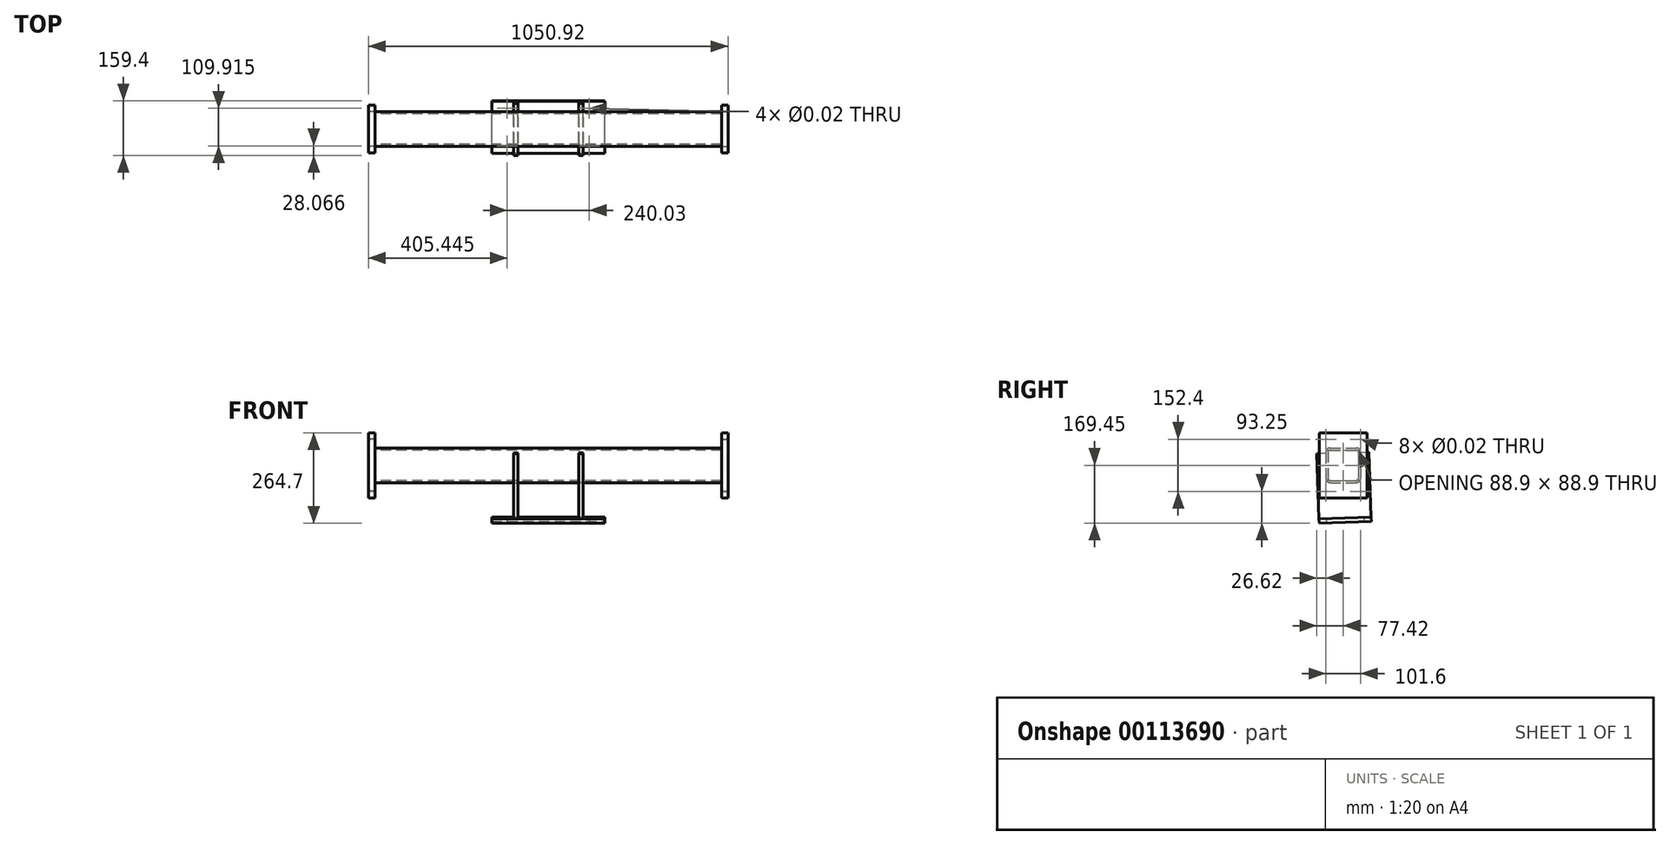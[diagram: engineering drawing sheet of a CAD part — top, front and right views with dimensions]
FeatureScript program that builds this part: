
annotation { "Feature Type Name" : "Feature", "Feature Type Description" : "" }
export const myFeature = defineFeature(function(context is Context, id is Id, definition is map)
    precondition{}
    {
        {
            var Q0;
            Q0=qCreatedBy(makeId("Right.planeOp"),FACE);
            var sketch = newSketch(context, id + "F0", { "sketchPlane" : qUnion([Q0])});
            skLineSegment(sketch, "E0.bottom", {"start": v(-38.1, 50.8) * mm, "end": v(38.1, 50.8) * mm});
            skLineSegment(sketch, "E0.top", {"start": v(-38.1, -50.8) * mm, "end": v(38.1, -50.8) * mm});
            skLineSegment(sketch, "E0.left", {"start": v(-50.8, 38.1) * mm, "end": v(-50.8, -38.1) * mm});
            skLineSegment(sketch, "E0.right", {"start": v(50.8, 38.1) * mm, "end": v(50.8, -38.1) * mm});
            skPoint(sketch, "E0.middle", {"position": v(0, 0) * mm});
            skPoint(sketch, "E1.visualSharp", {"position": v(-50.8, 50.8) * mm});
            skArc(sketch, "E1.filletArc", {"start": v(-38.1, 50.8) * mm, "mid": v(-47.08, 47.08) * mm, "end": v(-50.8, 38.1) * mm});
            skPoint(sketch, "E2.visualSharp", {"position": v(50.8, 50.8) * mm});
            skArc(sketch, "E2.filletArc", {"start": v(50.8, 38.1) * mm, "mid": v(47.08, 47.08) * mm, "end": v(38.1, 50.8) * mm});
            skPoint(sketch, "E3.visualSharp", {"position": v(50.8, -50.8) * mm});
            skArc(sketch, "E3.filletArc", {"start": v(38.1, -50.8) * mm, "mid": v(47.08, -47.08) * mm, "end": v(50.8, -38.1) * mm});
            skPoint(sketch, "E4.visualSharp", {"position": v(-50.8, -50.8) * mm});
            skArc(sketch, "E4.filletArc", {"start": v(-50.8, -38.1) * mm, "mid": v(-47.08, -47.08) * mm, "end": v(-38.1, -50.8) * mm});
            skArc(sketch, "E5.0", {"start": v(-38.1, 44.45) * mm, "mid": v(-42.6, 42.6) * mm, "end": v(-44.45, 38.1) * mm});
            skLineSegment(sketch, "E5.1", {"start": v(-44.45, 38.1) * mm, "end": v(-44.45, -38.1) * mm});
            skLineSegment(sketch, "E5.2", {"start": v(-38.1, 44.45) * mm, "end": v(38.1, 44.45) * mm});
            skArc(sketch, "E5.3", {"start": v(-44.45, -38.1) * mm, "mid": v(-42.6, -42.6) * mm, "end": v(-38.1, -44.45) * mm});
            skArc(sketch, "E5.4", {"start": v(44.45, 38.1) * mm, "mid": v(42.6, 42.6) * mm, "end": v(38.1, 44.45) * mm});
            skLineSegment(sketch, "E5.5", {"start": v(44.45, 38.1) * mm, "end": v(44.45, -38.1) * mm});
            skArc(sketch, "E5.6", {"start": v(38.1, -44.45) * mm, "mid": v(42.6, -42.6) * mm, "end": v(44.45, -38.1) * mm});
            skLineSegment(sketch, "E5.7", {"start": v(-38.1, -44.45) * mm, "end": v(38.1, -44.45) * mm});
            skSolve(sketch);
        }
        {
            var Q0;
            Q0 = qSketchRegion(id + "F0", true);
            extrude(context, id + "F1", {"entities" : qUnion([Q0]), "endBound" : BoundingType.SYMMETRIC, "depth" : 1012.82 * mm});
        }
        {
            var Q0;
            Q0=makeQuery(id+"F1.opExtrude","CAP_FACE",FACE,{"disambiguationData":[OSD([sQuery(id+"F0.wireOp",EDGE,"E0.bottom"),sQuery(id+"F0.wireOp",EDGE,"E0.top"),sQuery(id+"F0.wireOp",EDGE,"E0.left"),sQuery(id+"F0.wireOp",EDGE,"E0.right"),sQuery(id+"F0.wireOp",EDGE,"E1.filletArc"),sQuery(id+"F0.wireOp",EDGE,"E2.filletArc"),sQuery(id+"F0.wireOp",EDGE,"E3.filletArc"),sQuery(id+"F0.wireOp",EDGE,"E4.filletArc"),sQuery(id+"F0.wireOp",EDGE,"E5.0"),sQuery(id+"F0.wireOp",EDGE,"E5.1"),sQuery(id+"F0.wireOp",EDGE,"E5.2"),sQuery(id+"F0.wireOp",EDGE,"E5.3"),sQuery(id+"F0.wireOp",EDGE,"E5.4"),sQuery(id+"F0.wireOp",EDGE,"E5.5"),sQuery(id+"F0.wireOp",EDGE,"E5.6"),sQuery(id+"F0.wireOp",EDGE,"E5.7")])],"isStart":false});
            var sketch = newSketch(context, id + "F2", { "sketchPlane" : qUnion([Q0])});
            skLineSegment(sketch, "E6.bottom", {"start": v(-69.85, 95.25) * mm, "end": v(69.85, 95.25) * mm});
            skLineSegment(sketch, "E6.top", {"start": v(-69.85, -95.25) * mm, "end": v(69.85, -95.25) * mm});
            skLineSegment(sketch, "E6.left", {"start": v(-69.85, 95.25) * mm, "end": v(-69.85, -95.25) * mm});
            skLineSegment(sketch, "E6.right", {"start": v(69.85, 95.25) * mm, "end": v(69.85, -95.25) * mm});
            skPoint(sketch, "E6.middle", {"position": v(0, 0) * mm});
            skSolve(sketch);
        }
        {
            var Q0;
            Q0 = qSketchRegion(id + "F2", true);
            extrude(context, id + "F3", {"entities" : qUnion([Q0]), "depth" : 19.05 * mm});
        }
        {
            var Q0;
            Q0=makeQuery(id+"F3.opExtrude","CAP_FACE",FACE,{"disambiguationData":[OSD([sQuery(id+"F2.wireOp",EDGE,"E6.bottom"),sQuery(id+"F2.wireOp",EDGE,"E6.top"),sQuery(id+"F2.wireOp",EDGE,"E6.left"),sQuery(id+"F2.wireOp",EDGE,"E6.right")])],"isStart":false});
            var sketch = newSketch(context, id + "F4", { "sketchPlane" : qUnion([Q0])});
            skLineSegment(sketch, "E7.bottom", {"start": v(-50.8, 76.2) * mm, "end": v(50.8, 76.2) * mm, "construction": true});
            skLineSegment(sketch, "E7.top", {"start": v(-50.8, -76.2) * mm, "end": v(50.8, -76.2) * mm, "construction": true});
            skLineSegment(sketch, "E7.left", {"start": v(-50.8, 76.2) * mm, "end": v(-50.8, -76.2) * mm, "construction": true});
            skLineSegment(sketch, "E7.right", {"start": v(50.8, 76.2) * mm, "end": v(50.8, -76.2) * mm, "construction": true});
            skPoint(sketch, "E7.middle", {"position": v(0, 0) * mm});
            skPoint(sketch, "E8", {"position": v(-50.8, 76.2) * mm});
            skPoint(sketch, "E9", {"position": v(50.8, 76.2) * mm});
            skPoint(sketch, "E10", {"position": v(50.8, -76.2) * mm});
            skPoint(sketch, "E11", {"position": v(-50.8, -76.2) * mm});
            skSolve(sketch);
        }
        {
            var Q0;
            Q0=sQuery(id+"F4.wireOp",VERTEX,"E8");
            var Q1;
            Q1=sQuery(id+"F4.wireOp",VERTEX,"E9");
            var Q2;
            Q2=sQuery(id+"F4.wireOp",VERTEX,"E11");
            var Q3;
            Q3=sQuery(id+"F4.wireOp",VERTEX,"E10");
            var Q4;
            Q4=makeQuery(id+"F3.opExtrude","SWEPT_BODY",BODY,{"disambiguationData":[OSD([sQuery(id+"F2.wireOp",EDGE,"E6.bottom"),sQuery(id+"F2.wireOp",EDGE,"E6.top"),sQuery(id+"F2.wireOp",EDGE,"E6.left"),sQuery(id+"F2.wireOp",EDGE,"E6.right")])]});
            hole(context, id + "F5", {"style" : HoleStyle.SIMPLE, "endStyle" : HoleEndStyle.THROUGH, "standardTappedOrClearance" : lookupTablePath({ "standard" : "ANSI", "size" : "5/8 (0.62)", "type" : "Drilled" }), "standardBlindInLast" : lookupTablePath({ "standard" : "ANSI", "size" : "5/8", "type" : "Drilled" }), "holeDiameter" : 5 / 203.2 * mm, "locations" : qUnion([Q0, Q1, Q2, Q3]), "scope" : qUnion([Q4]), "isTappedThrough" : true});
        }
        {
            var Q0;
            Q0=makeQuery(id+"F3.opExtrude","SWEPT_BODY",BODY,{"disambiguationData":[OSD([sQuery(id+"F2.wireOp",EDGE,"E6.bottom"),sQuery(id+"F2.wireOp",EDGE,"E6.top"),sQuery(id+"F2.wireOp",EDGE,"E6.left"),sQuery(id+"F2.wireOp",EDGE,"E6.right")])]});
            var Q1;
            Q1=qCreatedBy(makeId("Right.planeOp"),FACE);
            mirror(context, id + "F6", {"entities" : qUnion([Q0]), "mirrorPlane" : qUnion([Q1])});
        }
        {
            var Q0;
            Q0=qCreatedBy(makeId("Right.planeOp"),FACE);
            cPlane(context, id + "F7", {"entities" : qUnion([Q0]), "cplaneType" : CPlaneType.OFFSET, "offset" : 88.9 * mm, "width" : 152.4 * mm, "height" : 152.4 * mm});
        }
        {
            var Q0;
            Q0=qCreatedBy(id+"F7.planeOp",FACE);
            var sketch = newSketch(context, id + "F8", { "sketchPlane" : qUnion([Q0])});
            skLineSegment(sketch, "E12", {"start": v(0, 0) * mm, "end": v(10.06, -288.01) * mm, "construction": true});
            skLineSegment(sketch, "E13", {"start": v(0, 0) * mm, "end": v(0, -287.93) * mm, "construction": true});
            skLineSegment(sketch, "E14.0", {"start": v(74.89, 38.94) * mm, "end": v(81.53, -151.44) * mm});
            skLineSegment(sketch, "E15.0", {"start": v(50.8, 38.1) * mm, "end": v(50.8, -38.1) * mm});
            skLineSegment(sketch, "E16.0", {"start": v(-50.8, 38.1) * mm, "end": v(-50.8, -38.1) * mm});
            skLineSegment(sketch, "E17", {"start": v(-133, 38.1) * mm, "end": v(-50.8, 38.1) * mm, "construction": true});
            skLineSegment(sketch, "E18.trimOffspring", {"start": v(50.8, 38.1) * mm, "end": v(138.85, 38.1) * mm, "construction": true});
            skLineSegment(sketch, "E19.MirrorCS", {"start": v(-77.42, 33.62) * mm, "end": v(-70.77, -156.76) * mm});
            skLineSegment(sketch, "E20", {"start": v(81.53, -151.44) * mm, "end": v(-70.77, -156.76) * mm});
            skLineSegment(sketch, "E21.0", {"start": v(-50.8, 34.55) * mm, "end": v(-77.42, 33.62) * mm});
            skPoint(sketch, "E22.orphan", {"position": v(76.15, 2.66) * mm});
            skLineSegment(sketch, "E23", {"start": v(50.8, 38.1) * mm, "end": v(74.89, 38.94) * mm});
            skPoint(sketch, "E24.orphan", {"position": v(86.21, -285.35) * mm});
            skPoint(sketch, "E25.orphan", {"position": v(-66.1, -290.67) * mm});
            skPoint(sketch, "E26.orphan", {"position": v(-76.15, -2.66) * mm});
            skArc(sketch, "E27.0", {"start": v(-50.8, -38.1) * mm, "mid": v(-47.08, -47.08) * mm, "end": v(-38.1, -50.8) * mm});
            skLineSegment(sketch, "E28.0", {"start": v(-38.1, -50.8) * mm, "end": v(38.1, -50.8) * mm});
            skArc(sketch, "E29.0", {"start": v(38.1, -50.8) * mm, "mid": v(47.08, -47.08) * mm, "end": v(50.8, -38.1) * mm});
            skSolve(sketch);
        }
        {
            var Q0;
            Q0 = qSketchRegion(id + "F8", true);
            extrude(context, id + "F9", {"entities" : qUnion([Q0]), "depth" : 12.7 * mm});
        }
        {
            var Q0;
            Q0=makeQuery(id+"F9.opExtrude","SWEPT_BODY",BODY,{"disambiguationData":[OSD([sQuery(id+"F8.wireOp",EDGE,"E14.0"),sQuery(id+"F8.wireOp",EDGE,"E15.0"),sQuery(id+"F8.wireOp",EDGE,"E16.0"),sQuery(id+"F8.wireOp",EDGE,"E19.MirrorCS"),sQuery(id+"F8.wireOp",EDGE,"E20"),sQuery(id+"F8.wireOp",EDGE,"E21.0"),sQuery(id+"F8.wireOp",EDGE,"E23"),sQuery(id+"F8.wireOp",EDGE,"E27.0"),sQuery(id+"F8.wireOp",EDGE,"E28.0"),sQuery(id+"F8.wireOp",EDGE,"E29.0")])]});
            var Q1;
            Q1=qCreatedBy(makeId("Right.planeOp"),FACE);
            mirror(context, id + "F10", {"entities" : qUnion([Q0]), "mirrorPlane" : qUnion([Q1])});
        }
        {
            var Q0;
            Q0=makeQuery(id+"F9.opExtrude","SWEPT_FACE",FACE,{"disambiguationData":[OSD([sQuery(id+"F8.wireOp",EDGE,"E20")])]});
            var sketch = newSketch(context, id + "F11", { "sketchPlane" : qUnion([Q0])});
            skLineSegment(sketch, "E30.0.0", {"start": v(-88.9, -76.2) * mm, "end": v(-88.9, 76.2) * mm, "construction": true});
            skLineSegment(sketch, "E30.0.1", {"start": v(-88.9, 76.2) * mm, "end": v(-101.6, 76.2) * mm, "construction": true});
            skLineSegment(sketch, "E30.0.2", {"start": v(-101.6, 76.2) * mm, "end": v(-101.6, -76.2) * mm, "construction": true});
            skLineSegment(sketch, "E30.0.3", {"start": v(-101.6, -76.2) * mm, "end": v(-88.9, -76.2) * mm, "construction": true});
            skLineSegment(sketch, "E31.0.1", {"start": v(88.9, -76.2) * mm, "end": v(88.9, 76.2) * mm, "construction": true});
            skLineSegment(sketch, "E31.0.3", {"start": v(88.9, 76.2) * mm, "end": v(88.9, 49.56) * mm, "construction": true});
            skLineSegment(sketch, "E31.0.4", {"start": v(88.9, 49.56) * mm, "end": v(88.9, 52.1) * mm, "construction": true});
            skLineSegment(sketch, "E31.0.5", {"start": v(88.9, 52.1) * mm, "end": v(88.9, 39.85) * mm, "construction": true});
            skLineSegment(sketch, "E31.0.6", {"start": v(88.9, 39.85) * mm, "end": v(88.9, -36.3) * mm, "construction": true});
            skLineSegment(sketch, "E31.0.7", {"start": v(88.9, -36.3) * mm, "end": v(88.9, -49.44) * mm, "construction": true});
            skLineSegment(sketch, "E31.0.8", {"start": v(88.9, -49.44) * mm, "end": v(88.9, -52.1) * mm, "construction": true});
            skLineSegment(sketch, "E31.0.9", {"start": v(88.9, -52.1) * mm, "end": v(88.9, -76.2) * mm, "construction": true});
            skLineSegment(sketch, "E32.0.0", {"start": v(88.9, 76.2) * mm, "end": v(88.9, -76.2) * mm, "construction": true});
            skLineSegment(sketch, "E32.0.1", {"start": v(88.9, -76.2) * mm, "end": v(101.6, -76.2) * mm, "construction": true});
            skLineSegment(sketch, "E32.0.2", {"start": v(101.6, -76.2) * mm, "end": v(101.6, 76.2) * mm, "construction": true});
            skLineSegment(sketch, "E32.0.3", {"start": v(101.6, 76.2) * mm, "end": v(88.9, 76.2) * mm, "construction": true});
            skLineSegment(sketch, "E33", {"start": v(-101.6, 0) * mm, "end": v(101.6, 0) * mm, "construction": true});
            skLineSegment(sketch, "E34.bottom", {"start": v(-165.1, 76.2) * mm, "end": v(165.1, 76.2) * mm});
            skLineSegment(sketch, "E34.top", {"start": v(-165.1, -76.2) * mm, "end": v(165.1, -76.2) * mm});
            skLineSegment(sketch, "E34.left", {"start": v(-165.1, 76.2) * mm, "end": v(-165.1, -76.2) * mm});
            skLineSegment(sketch, "E34.right", {"start": v(165.1, 76.2) * mm, "end": v(165.1, -76.2) * mm});
            skPoint(sketch, "E34.middle", {"position": v(0, 0) * mm});
            skSolve(sketch);
        }
        {
            var Q0;
            Q0 = qSketchRegion(id + "F11", true);
            extrude(context, id + "F12", {"entities" : qUnion([Q0]), "depth" : 12.7 * mm});
        }
        {
            var Q0;
            Q0=makeQuery(id+"F12.opExtrude","CAP_FACE",FACE,{"disambiguationData":[OSD([sQuery(id+"F11.wireOp",EDGE,"E34.bottom"),sQuery(id+"F11.wireOp",EDGE,"E34.top"),sQuery(id+"F11.wireOp",EDGE,"E34.left"),sQuery(id+"F11.wireOp",EDGE,"E34.right")])],"isStart":false});
            var sketch = newSketch(context, id + "F13", { "sketchPlane" : qUnion([Q0])});
            skLineSegment(sketch, "E35.0.0", {"start": v(165.1, 76.2) * mm, "end": v(-165.1, 76.2) * mm, "construction": true});
            skLineSegment(sketch, "E35.0.1", {"start": v(-165.1, 76.2) * mm, "end": v(-165.1, -76.2) * mm, "construction": true});
            skLineSegment(sketch, "E35.0.2", {"start": v(-165.1, -76.2) * mm, "end": v(165.1, -76.2) * mm, "construction": true});
            skLineSegment(sketch, "E35.0.3", {"start": v(165.1, -76.2) * mm, "end": v(165.1, 76.2) * mm, "construction": true});
            skLineSegment(sketch, "E36", {"start": v(-165.1, 76.2) * mm, "end": v(165.1, -76.2) * mm, "construction": true});
            skLineSegment(sketch, "E37.bottom", {"start": v(-120.01, -55) * mm, "end": v(120.02, -55) * mm, "construction": true});
            skLineSegment(sketch, "E37.top", {"start": v(-120.01, 55) * mm, "end": v(120.02, 55) * mm, "construction": true});
            skLineSegment(sketch, "E37.left", {"start": v(-120.01, -55) * mm, "end": v(-120.01, 55) * mm, "construction": true});
            skLineSegment(sketch, "E37.right", {"start": v(120.02, -55) * mm, "end": v(120.02, 55) * mm, "construction": true});
            skPoint(sketch, "E37.middle", {"position": v(0, 0) * mm});
            skPoint(sketch, "E38", {"position": v(-120.01, 55) * mm});
            skPoint(sketch, "E39", {"position": v(-120.01, -55) * mm});
            skPoint(sketch, "E40", {"position": v(120.02, -55) * mm});
            skPoint(sketch, "E41", {"position": v(120.02, 55) * mm});
            skSolve(sketch);
        }
        {
            var Q0;
            Q0=sQuery(id+"F13.wireOp",VERTEX,"E38");
            var Q1;
            Q1=sQuery(id+"F13.wireOp",VERTEX,"E41");
            var Q2;
            Q2=sQuery(id+"F13.wireOp",VERTEX,"E40");
            var Q3;
            Q3=sQuery(id+"F13.wireOp",VERTEX,"E39");
            var Q4;
            Q4=makeQuery(id+"F12.opExtrude","SWEPT_BODY",BODY,{"disambiguationData":[OSD([sQuery(id+"F11.wireOp",EDGE,"E34.bottom"),sQuery(id+"F11.wireOp",EDGE,"E34.top"),sQuery(id+"F11.wireOp",EDGE,"E34.left"),sQuery(id+"F11.wireOp",EDGE,"E34.right")])]});
            hole(context, id + "F14", {"style" : HoleStyle.SIMPLE, "endStyle" : HoleEndStyle.THROUGH, "standardTappedOrClearance" : lookupTablePath({ "standard" : "ANSI", "size" : "7/16 (0.44)", "type" : "Drilled" }), "standardBlindInLast" : lookupTablePath({ "standard" : "ANSI", "size" : "7/16", "type" : "Drilled" }), "holeDiameter" : 7 / 406.4 * mm, "locations" : qUnion([Q0, Q1, Q2, Q3]), "scope" : qUnion([Q4]), "isTappedThrough" : true});
        }
    });
